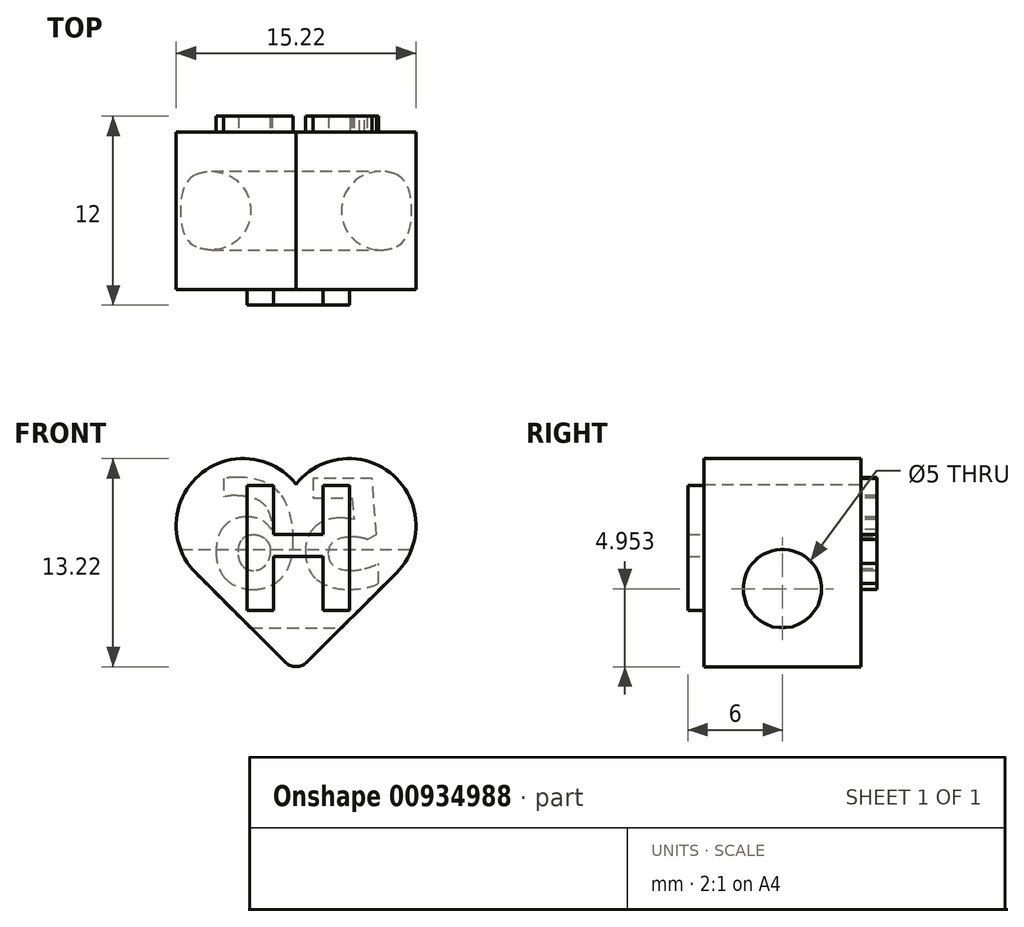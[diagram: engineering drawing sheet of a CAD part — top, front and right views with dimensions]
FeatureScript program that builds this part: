
annotation { "Feature Type Name" : "Feature", "Feature Type Description" : "" }
export const myFeature = defineFeature(function(context is Context, id is Id, definition is map)
    precondition{}
    {
        {
            var Q0;
            Q0=qCreatedBy(makeId("Front.planeOp"),FACE);
            var sketch = newSketch(context, id + "F0", { "sketchPlane" : qUnion([Q0])});
            skLineSegment(sketch, "E0", {"start": v(0, -5) * mm, "end": v(-6.36, 1.37) * mm});
            skArc(sketch, "E1", {"start": v(0, 7) * mm, "mid": v(-6.18, 7.57) * mm, "end": v(-6.36, 1.37) * mm});
            skLineSegment(sketch, "E2", {"start": v(0, -5) * mm, "end": v(0, 7) * mm});
            skArc(sketch, "E3.MirrorCS", {"start": v(0, 7) * mm, "mid": v(6.18, 7.57) * mm, "end": v(6.36, 1.37) * mm});
            skLineSegment(sketch, "E4.MirrorCS", {"start": v(0, -5) * mm, "end": v(6.36, 1.37) * mm});
            skSolve(sketch);
        }
        {
            var Q0;
            Q0 = qSketchRegion(id + "F0", true);
            extrude(context, id + "F1", {"entities" : qUnion([Q0]), "depth" : 10 * mm, "offsetDistance" : 25 * mm});
        }
        {
            var Q0;
            Q0=makeQuery(id+"F1.opExtrude","CAP_FACE",FACE,{"disambiguationData":[OSD([sQuery(id+"F0.wireOp",EDGE,"E0"),sQuery(id+"F0.wireOp",EDGE,"E1"),sQuery(id+"F0.wireOp",EDGE,"E3.MirrorCS"),sQuery(id+"F0.wireOp",EDGE,"E4.MirrorCS")])],"isStart":false});
            var sketch = newSketch(context, id + "F2", { "sketchPlane" : qUnion([Q0])});
            skText(sketch, "E5", { "text": "H", "fontName": "OpenSans-Bold.ttf"});
            const initialGuessF2  = {"E5": [-0.0041, -0.001, 1, 0, 0.008]};
            skSetInitialGuess(sketch, initialGuessF2);
            skSolve(sketch);
        }
        {
            var Q0;
            Q0 = qSketchRegion(id + "F2", true);
            extrude(context, id + "F3", {"entities" : qUnion([Q0]), "operationType" : NewBodyOperationType.ADD, "depth" : 1 * mm, "offsetDistance" : 25 * mm});
        }
        {
            var Q0;
            Q0=qCreatedBy(makeId("Front.planeOp"),FACE);
            cPlane(context, id + "F4", {"entities" : qUnion([Q0]), "cplaneType" : CPlaneType.OFFSET, "offset" : 4 * mm, "width" : 150 * mm, "height" : 150 * mm});
        }
        {
            var Q0;
            Q0=qCreatedBy(makeId("Right.planeOp"),FACE);
            var sketch = newSketch(context, id + "F5", { "sketchPlane" : qUnion([Q0])});
            skCircle(sketch, "E6", {"center": v(-5, 0.37) * mm, "radius": 2.5 * mm});
            skSolve(sketch);
        }
        {
            var Q0;
            Q0 = qSketchRegion(id + "F5", true);
            extrude(context, id + "F6", {"entities" : qUnion([Q0]), "operationType" : NewBodyOperationType.REMOVE, "endBound" : BoundingType.SYMMETRIC, "oppositeDirection" : true, "depth" : 25 * mm, "offsetDistance" : 25 * mm});
        }
        {
            var Q0;
            Q0=makeQuery(id+"F1.opExtrude","SWEPT_EDGE",EDGE,{"disambiguationData":[OSD([sQuery(id+"F0.wireOp",EDGE,"E0"),sQuery(id+"F0.wireOp",EDGE,"E2"),sQuery(id+"F0.wireOp",EDGE,"E4.MirrorCS")])]});
            fillet(context, id + "F7", {"entities" : qUnion([Q0]), "radius" : 1 * mm, "tangentPropagation" : true, "allowEdgeOverflow" : false});
        }
        {
            var Q0;
            Q0=makeQuery(id+"F1.opExtrude","CAP_FACE",FACE,{"disambiguationData":[OSD([sQuery(id+"F0.wireOp",EDGE,"E0"),sQuery(id+"F0.wireOp",EDGE,"E1"),sQuery(id+"F0.wireOp",EDGE,"E3.MirrorCS"),sQuery(id+"F0.wireOp",EDGE,"E4.MirrorCS")])],"isStart":true});
            var sketch = newSketch(context, id + "F8", { "sketchPlane" : qUnion([Q0])});
            skText(sketch, "E7", { "text": "56\n", "fontName": "OpenSans-Bold.ttf"});
            const initialGuessF8  = {"E7": [-0.00571, 0.00043, 1, 0, 0.007]};
            skSetInitialGuess(sketch, initialGuessF8);
            skSolve(sketch);
        }
        {
            var Q0;
            Q0 = qSketchRegion(id + "F8", true);
            extrude(context, id + "F9", {"entities" : qUnion([Q0]), "operationType" : NewBodyOperationType.ADD, "depth" : 1 * mm, "offsetDistance" : 25 * mm});
        }
    });
